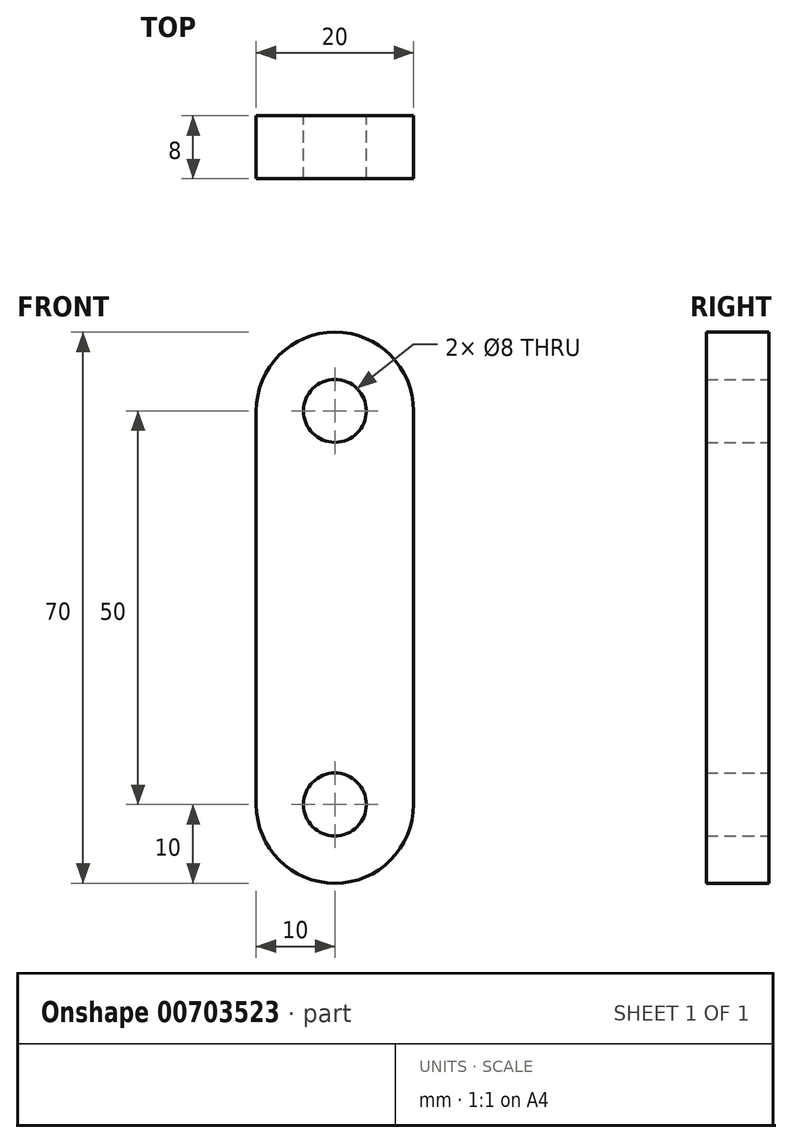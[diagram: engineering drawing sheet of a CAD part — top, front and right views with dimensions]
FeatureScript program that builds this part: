
annotation { "Feature Type Name" : "Feature", "Feature Type Description" : "" }
export const myFeature = defineFeature(function(context is Context, id is Id, definition is map)
    precondition{}
    {
        {
            var Q0;
            Q0=qCreatedBy(makeId("Front.planeOp"),FACE);
            var sketch = newSketch(context, id + "F0", { "sketchPlane" : qUnion([Q0])});
            skLineSegment(sketch, "E0.bottom", {"start": v(-10, 0) * mm, "end": v(10, 0) * mm});
            skLineSegment(sketch, "E0.left", {"start": v(-10, 0) * mm, "end": v(-10, 25) * mm});
            skLineSegment(sketch, "E0.right", {"start": v(10, 0) * mm, "end": v(10, 25) * mm});
            skArc(sketch, "E1", {"start": v(-10, 25) * mm, "mid": v(0, 35) * mm, "end": v(10, 25) * mm});
            skCircle(sketch, "E2", {"center": v(0, 25) * mm, "radius": 4 * mm});
            skLineSegment(sketch, "E3.MirrorCS", {"start": v(10, 0) * mm, "end": v(10, -25) * mm});
            skCircle(sketch, "E4.MirrorC", {"center": v(0, -25) * mm, "radius": 4 * mm});
            skArc(sketch, "E5.MirrorCS", {"start": v(-10, -25) * mm, "mid": v(0, -35) * mm, "end": v(10, -25) * mm});
            skLineSegment(sketch, "E6.MirrorCS", {"start": v(-10, 0) * mm, "end": v(-10, -25) * mm});
            skSolve(sketch);
        }
        {
            var Q0;
            Q0=makeQuery(id+"F0.imprint","IMPRINT",FACE,{"disambiguationData":[TD([[makeQuery(id+"F0.imprint","IMPRINT",EDGE,{"derivedFrom":sQuery(id+"F0.wireOp",EDGE,"E0.bottom")}),1.0]])]});
            var Q1;
            Q1=makeQuery(id+"F0.imprint","IMPRINT",FACE,{"disambiguationData":[TD([[makeQuery(id+"F0.imprint","IMPRINT",EDGE,{"derivedFrom":sQuery(id+"F0.wireOp",EDGE,"E0.bottom")}),-1.0]])]});
            extrude(context, id + "F1", {"entities" : qUnion([Q0, Q1]), "depth" : 8 * mm, "offsetDistance" : 25 * mm});
        }
    });
